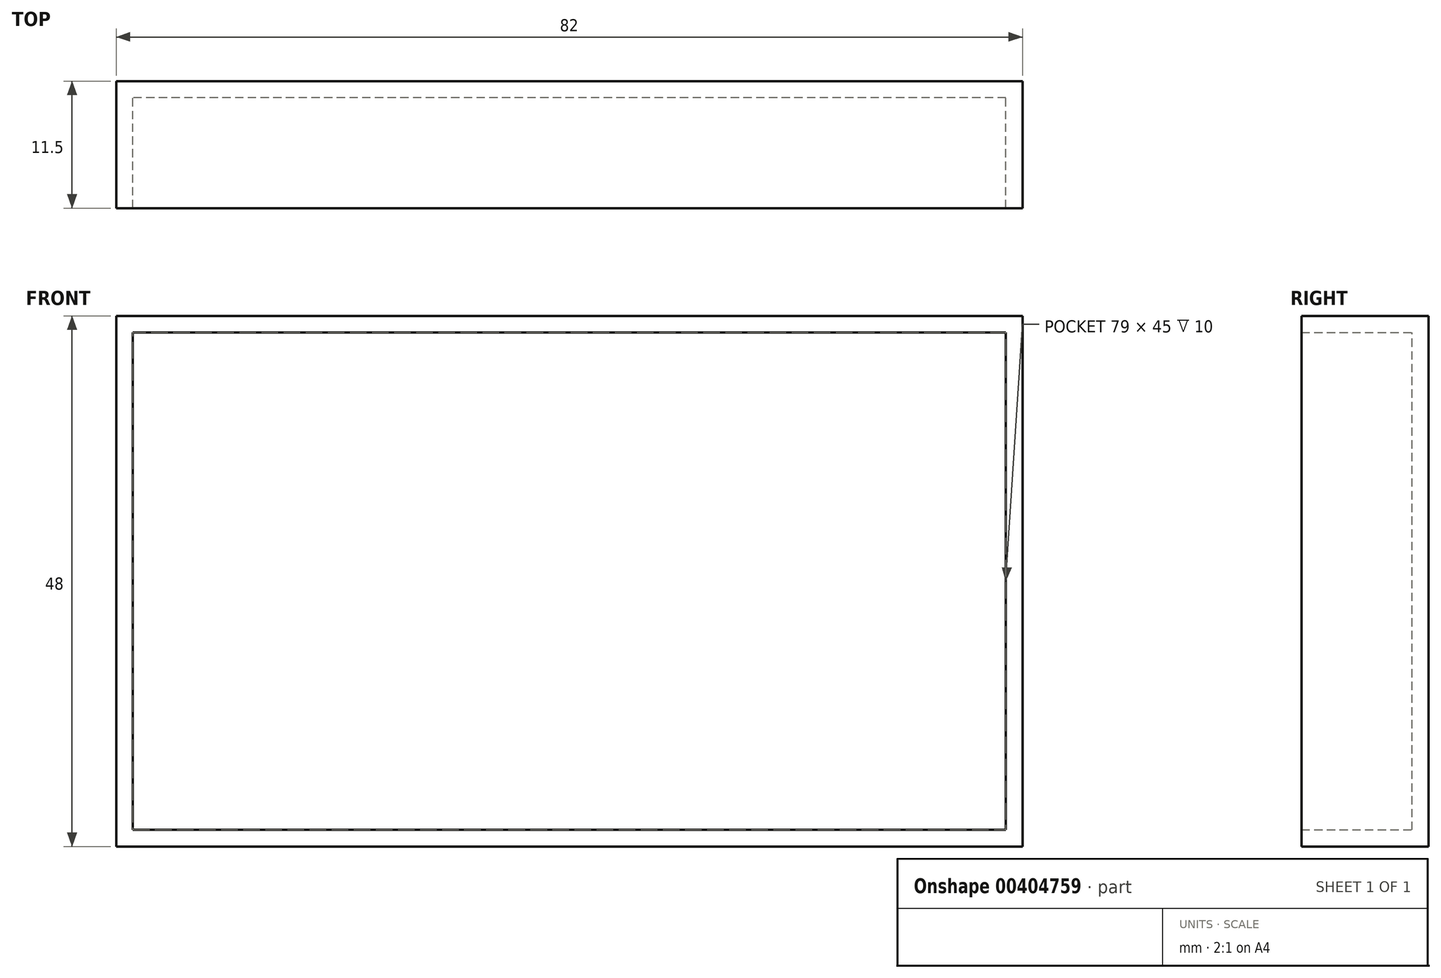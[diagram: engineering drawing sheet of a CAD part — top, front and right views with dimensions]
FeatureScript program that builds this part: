
annotation { "Feature Type Name" : "Feature", "Feature Type Description" : "" }
export const myFeature = defineFeature(function(context is Context, id is Id, definition is map)
    precondition{}
    {
        {
            var Q0;
            Q0=qCreatedBy(makeId("Front.planeOp"),FACE);
            var sketch = newSketch(context, id + "F0", { "sketchPlane" : qUnion([Q0])});
            skLineSegment(sketch, "E0.bottom", {"start": v(-39.5, 22.5) * mm, "end": v(39.5, 22.5) * mm});
            skLineSegment(sketch, "E0.top", {"start": v(-39.5, -22.5) * mm, "end": v(39.5, -22.5) * mm});
            skLineSegment(sketch, "E0.left", {"start": v(-39.5, 22.5) * mm, "end": v(-39.5, -22.5) * mm});
            skLineSegment(sketch, "E0.right", {"start": v(39.5, 22.5) * mm, "end": v(39.5, -22.5) * mm});
            skLineSegment(sketch, "E1.0", {"start": v(-41, 24) * mm, "end": v(41, 24) * mm});
            skLineSegment(sketch, "E1.1", {"start": v(-41, 24) * mm, "end": v(-41, -24) * mm});
            skLineSegment(sketch, "E1.2", {"start": v(-41, -24) * mm, "end": v(41, -24) * mm});
            skLineSegment(sketch, "E1.3", {"start": v(41, 24) * mm, "end": v(41, -24) * mm});
            skSolve(sketch);
        }
        {
            var Q0;
            Q0=makeQuery(id+"F0.imprint","IMPRINT",FACE,{"disambiguationData":[TD([[makeQuery(id+"F0.imprint","IMPRINT",EDGE,{"derivedFrom":sQuery(id+"F0.wireOp",EDGE,"E0.bottom")}),1.0]])]});
            var Q1;
            Q1=makeQuery(id+"F0.imprint","IMPRINT",FACE,{"disambiguationData":[TD([[makeQuery(id+"F0.imprint","IMPRINT",EDGE,{"derivedFrom":sQuery(id+"F0.wireOp",EDGE,"E0.bottom")}),-1.0]])]});
            extrude(context, id + "F1", {"entities" : qUnion([Q0, Q1]), "depth" : 1.5 * mm});
        }
        {
            var Q0;
            Q0 = qSketchRegion(id + "F0", true);
            extrude(context, id + "F2", {"entities" : qUnion([Q0]), "operationType" : NewBodyOperationType.ADD, "depth" : 11.5 * mm});
        }
    });
